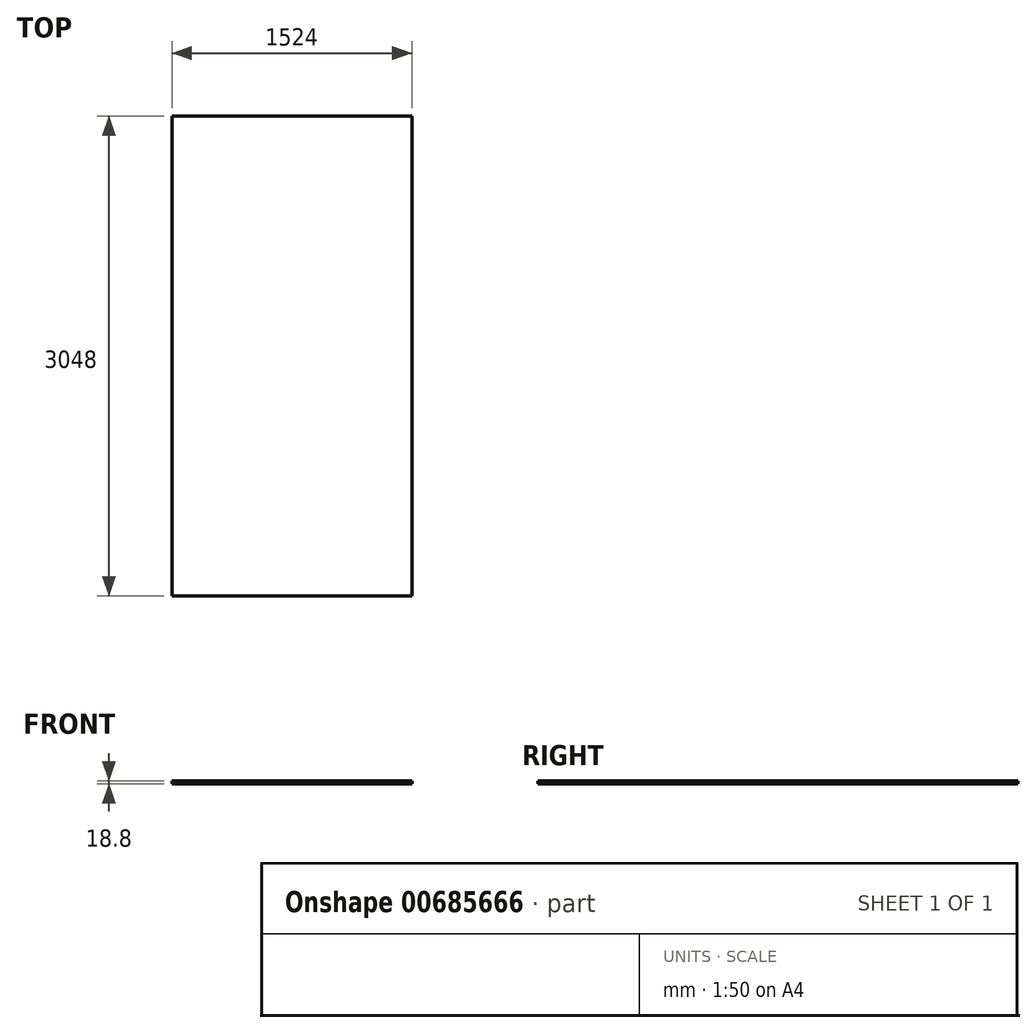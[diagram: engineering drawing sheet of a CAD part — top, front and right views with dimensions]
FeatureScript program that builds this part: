
annotation { "Feature Type Name" : "Feature", "Feature Type Description" : "" }
export const myFeature = defineFeature(function(context is Context, id is Id, definition is map)
    precondition{}
    {
        {
            var Q0;
            Q0=qCreatedBy(makeId("Top.planeOp"),FACE);
            var sketch = newSketch(context, id + "F0", { "sketchPlane" : qUnion([Q0])});
            skLineSegment(sketch, "E0.bottom", {"start": v(-762, 1524) * mm, "end": v(762, 1524) * mm});
            skLineSegment(sketch, "E0.top", {"start": v(-762, -1524) * mm, "end": v(762, -1524) * mm});
            skLineSegment(sketch, "E0.left", {"start": v(-762, 1524) * mm, "end": v(-762, -1524) * mm});
            skLineSegment(sketch, "E0.right", {"start": v(762, 1524) * mm, "end": v(762, -1524) * mm});
            skPoint(sketch, "E0.middle", {"position": v(0, 0) * mm});
            skSolve(sketch);
        }
        {
            var Q0;
            Q0 = qSketchRegion(id + "F0", true);
            extrude(context, id + "F1", {"entities" : qUnion([Q0]), "depth" : 18.8 * mm, "offsetDistance" : 30.48 * mm});
        }
    });
